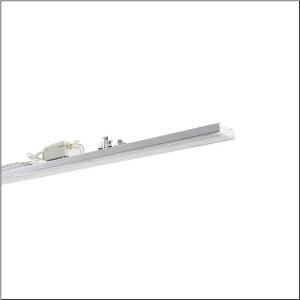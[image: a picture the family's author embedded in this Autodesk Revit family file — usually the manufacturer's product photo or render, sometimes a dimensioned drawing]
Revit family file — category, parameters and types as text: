
# Revit family: licross_21_recessed_ho_52tl18dv4l2m
name_source: partatom
category: Lighting Fixtures
units: mm (PartAtom-declared; Revit-internal decimal feet)

## family parameters
Cut with Voids When Loaded = No
Host = Face
Light Source = No
Part Type = Normal
Room Calculation Point = No
Round Connector Dimension = Use Diameter
Shared = No

## types (1)
- --- (1 x LED, 22480 lm, 125.6 W, 4000K)
    Apparent Load = 126 VA
    CIE Flux Codes = 75 94 99 100 100
    Color Rendering = 80
    Color Temperature = 4000K
    Default Elevation = 1800 mm
    Description = Licross 21 Recessed HO, luminaire insert, of sheet steel, galvanised, coil coated, white, length: 2.250mm, width: 66mm, height: 67mm, LED rated luminous flux: 22.480lm, light colour: 840, SDCM (Standard Deviation of Colour Matching)MacAdam ≤ 3 SDCM (initial), control gear: DALI 2, with plug, 5-pole, with phase selection, mains connection: 220..240V, AC, 50/60Hz, rated input power: 126W, internal wiring halogen-free, primary light control with lens, of plastic, primary optical cover: cover, of PMMA, light emission: direct distribution, primary light characteristic: symmetric, protection rating (complete): IP40, insulation class (complete): insulation class I (protective earthing), certification: CE, ENEC, VDE, UKCA, protection symbol: D if used in an environment without relevant dust loads with corresponding accessories, impact resistance: IK06, permissible ambient temperature for indoor applications: -40..+30°C, corresponds to IFS (International Featured Standards) requirements for safety and quality in the food industry, reducing of maximum allowable ambient temperature of 5°C with ceiling mounting, LABS conformity tested according to VDMA 24364:2018-05, The light source and the operating device comply with the requirements of the Ecodesign Regulation (EU) 2019/2020 and are replaceable in accordance with this regulation, packaging unit: 1 piece
    Height = 58 mm
    Lamp = 1 x LED
    Lamp Light Flux = 22480 lm
    Lamp Power = 125.6 W
    Lamp count = 1
    Length = 2250 mm
    Luminous efficacy = 179 lm/W
    Manufacturer = Siteco
    ModVariant = No
    Model = 52TL18DV4L2M
    Mounting Place = Ceiling
    Mounting Type = Pendant
    Number of Poles = 1
    OnlyDefault = Yes
    Power Factor = 1
    Product Name = Licross 21 Recessed HO
    Product group = luminaire insert | ceiling pendant
    ProductGroupID = 901
    Protection Class = Protection class I
    Protection Degree = IP 40
    RLX_Detail_Level = 1
    RLX_Emergency_Light_Flux = 0 lm
    RLX_Emergency_Type = 0
    RLX_Emergency_Type_DB = No
    RlxData = <blob elided: 29921 chars, md5=cf3b203a>
    Socket = socket
    Standby Power = 0 W
    System Light Flux = 22480 lm
    System Power = 126 W
    Type Comments = factory setting: luminous flux: 100 % | dim-lin: 254 | 489 mA
    Type Image = l_1296930.jpg
    URL = http://relux.com
    VarID = @adj_127559
    Voltage = 0 V
    Weight = 0.00 kg
    Width = 66 mm

## geometry (parser evidence)
native form markers: Blend x4, Sweep x9
no freeform markers — native parametric forms only
